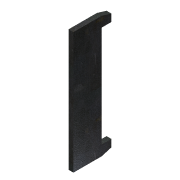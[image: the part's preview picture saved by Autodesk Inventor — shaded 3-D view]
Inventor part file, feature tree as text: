
AUTODESK INVENTOR PART (.ipt)
format: ipt  version: 2016 (Build 200138000, 138)  size: 90,112 bytes
history: native  units: mm
features: extrude x1, sketch x1
ambient origin geometry x8: Origin, YZ Plane, XZ Plane, XY Plane, X Axis, Y Axis, Z Axis, Center Point
bodies: Solid1 (feature_tree)
feature tree (2):
  extrude  "Extrusion1"  Depth=10.0mm TaperAngle=0.0deg
  sketch  "Sketch1"  dims[d0=62.0mm d2=10.0mm d3=0.0mm d4=15.0mm d5=15.0mm d6=208.0mm]
